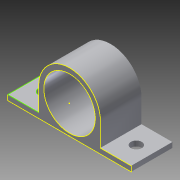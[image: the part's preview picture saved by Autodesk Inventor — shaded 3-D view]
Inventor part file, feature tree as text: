
AUTODESK INVENTOR PART (.ipt)
format: ipt  version: 2013 (Build 170138000, 138)  size: 151,552 bytes
history: native  units: in
note: dims shown in document units (in); Inventor stores cm internally (conversion verified against a paired STEP export)
features: sketch x6, extrude x2
ambient origin geometry x8: Origin, YZ Plane, XZ Plane, XY Plane, X Axis, Y Axis, Z Axis, Center Point
bodies: Solid1 (feature_tree)
feature tree (8):
  extrude  "Extrusion1"  Depth=1.5in
  extrude  "Extrusion2"  Depth=0.6875in
  sketch  "Sketch3"  dims[d4=1.25in]
  sketch  "Sketch4"  dims[d5=0.125in]
  sketch  "Sketch5"  dims[d6=1.0in d7=0.0in]
  sketch  "Sketch6"  dims[d8=0.266in d11=1.0in d12=0.0in d13=0.375in d14=0.266in d15=0.375in]
  sketch  "Sketch1"  dims[d0=1.5in d1=1.5in]
  sketch  "Sketch2"  dims[d2=0.125in d3=0.6875in]
